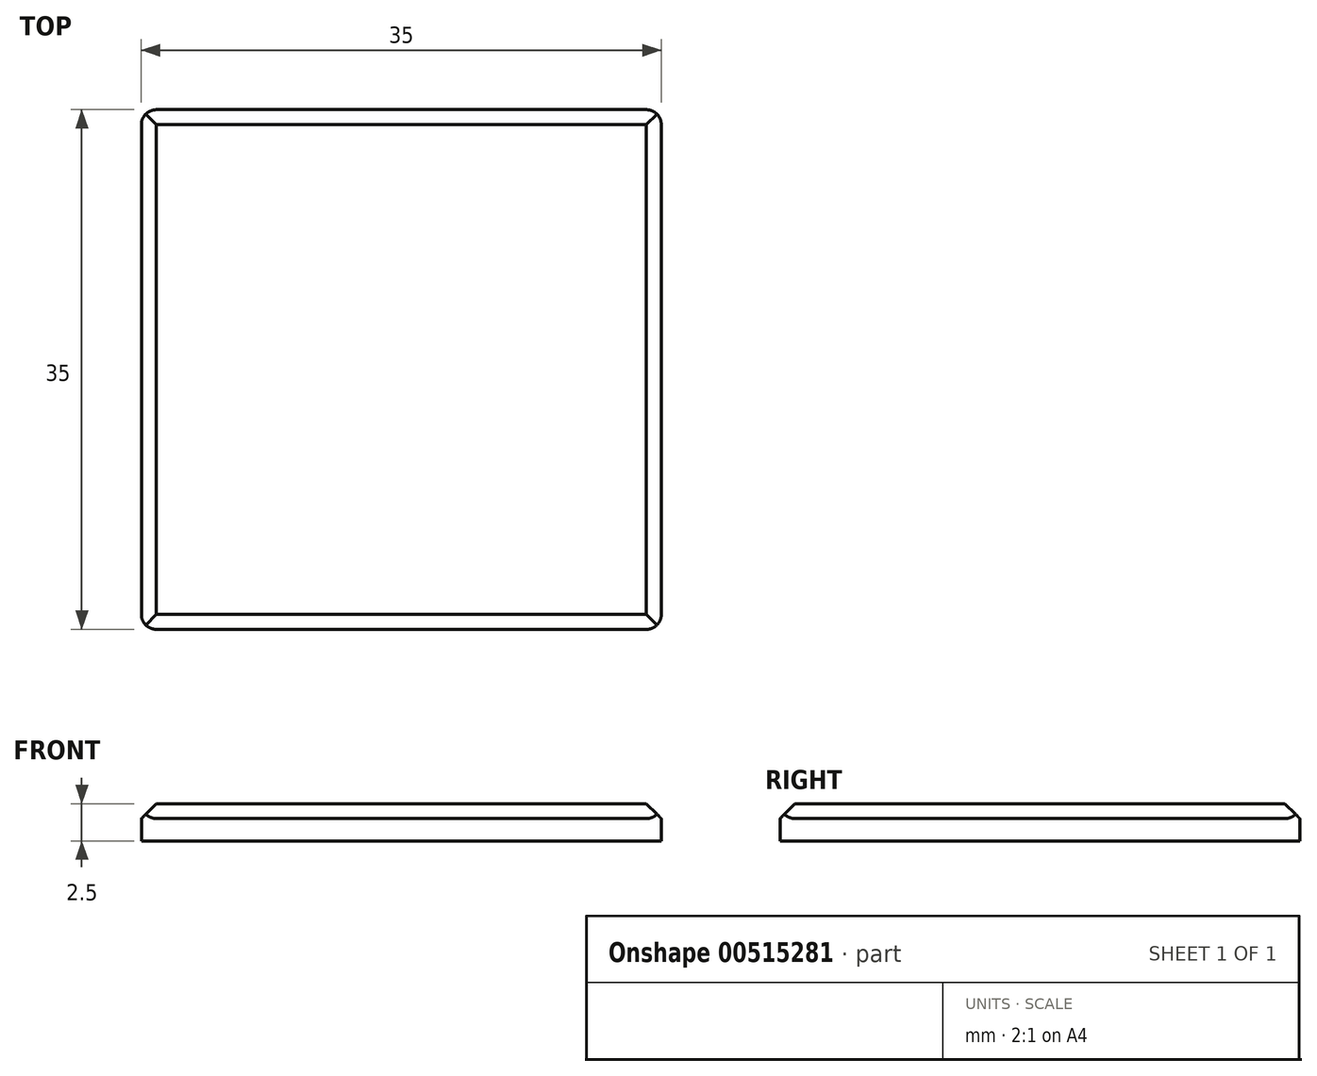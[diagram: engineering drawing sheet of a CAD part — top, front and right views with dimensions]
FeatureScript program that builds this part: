
annotation { "Feature Type Name" : "Feature", "Feature Type Description" : "" }
export const myFeature = defineFeature(function(context is Context, id is Id, definition is map)
    precondition{}
    {
        {
            var Q0;
            Q0=qCreatedBy(makeId("Top.planeOp"),FACE);
            var sketch = newSketch(context, id + "F0", { "sketchPlane" : qUnion([Q0])});
            skLineSegment(sketch, "E0.bottom", {"start": v(-24.97, -12.93) * mm, "end": v(10.03, -12.93) * mm});
            skLineSegment(sketch, "E0.top", {"start": v(-24.97, 22.07) * mm, "end": v(10.03, 22.07) * mm});
            skLineSegment(sketch, "E0.left", {"start": v(-24.97, -12.93) * mm, "end": v(-24.97, 22.07) * mm});
            skLineSegment(sketch, "E0.right", {"start": v(10.03, -12.93) * mm, "end": v(10.03, 22.07) * mm});
            skSolve(sketch);
        }
        {
            var Q0;
            Q0=makeQuery(id+"F0.imprint","IMPRINT",FACE,{"disambiguationData":[TD([[makeQuery(id+"F0.imprint","IMPRINT",EDGE,{"derivedFrom":sQuery(id+"F0.wireOp",EDGE,"E0.bottom")}),1.0]])]});
            extrude(context, id + "F1", {"entities" : qUnion([Q0]), "depth" : 2.5 * mm, "offsetDistance" : 25 * mm});
        }
        {
            var Q0;
            Q0=makeQuery(id+"F1.opExtrude","CAP_EDGE",EDGE,{"disambiguationData":[OSD([sQuery(id+"F0.wireOp",EDGE,"E0.bottom")])],"isStart":false});
            var Q1;
            Q1=makeQuery(id+"F1.opExtrude","CAP_EDGE",EDGE,{"disambiguationData":[OSD([sQuery(id+"F0.wireOp",EDGE,"E0.left")])],"isStart":false});
            var Q2;
            Q2=makeQuery(id+"F1.opExtrude","CAP_EDGE",EDGE,{"disambiguationData":[OSD([sQuery(id+"F0.wireOp",EDGE,"E0.top")])],"isStart":false});
            var Q3;
            Q3=makeQuery(id+"F1.opExtrude","CAP_EDGE",EDGE,{"disambiguationData":[OSD([sQuery(id+"F0.wireOp",EDGE,"E0.right")])],"isStart":false});
            chamfer(context, id + "F2", {"entities" : qUnion([Q0, Q1, Q2, Q3]), "width" : 1 * mm, "tangentPropagation" : true});
        }
        {
            var Q0;
            Q0=makeQuery(id+"F1.opExtrude","SWEPT_EDGE",EDGE,{"disambiguationData":[OSD([sQuery(id+"F0.wireOp",EDGE,"E0.bottom"),sQuery(id+"F0.wireOp",EDGE,"E0.left")])]});
            fillet(context, id + "F3", {"entities" : qUnion([Q0]), "radius" : 1 * mm, "tangentPropagation" : true, "allowEdgeOverflow" : false});
        }
        {
            var Q0;
            Q0=makeQuery(id+"F1.opExtrude","SWEPT_EDGE",EDGE,{"disambiguationData":[OSD([sQuery(id+"F0.wireOp",EDGE,"E0.top"),sQuery(id+"F0.wireOp",EDGE,"E0.left")])]});
            var Q1;
            Q1=makeQuery(id+"F1.opExtrude","SWEPT_EDGE",EDGE,{"disambiguationData":[OSD([sQuery(id+"F0.wireOp",EDGE,"E0.top"),sQuery(id+"F0.wireOp",EDGE,"E0.right")])]});
            var Q2;
            Q2=makeQuery(id+"F1.opExtrude","SWEPT_EDGE",EDGE,{"disambiguationData":[OSD([sQuery(id+"F0.wireOp",EDGE,"E0.bottom"),sQuery(id+"F0.wireOp",EDGE,"E0.right")])]});
            fillet(context, id + "F4", {"entities" : qUnion([Q0, Q1, Q2]), "radius" : 1 * mm, "tangentPropagation" : true, "allowEdgeOverflow" : false});
        }
    });
